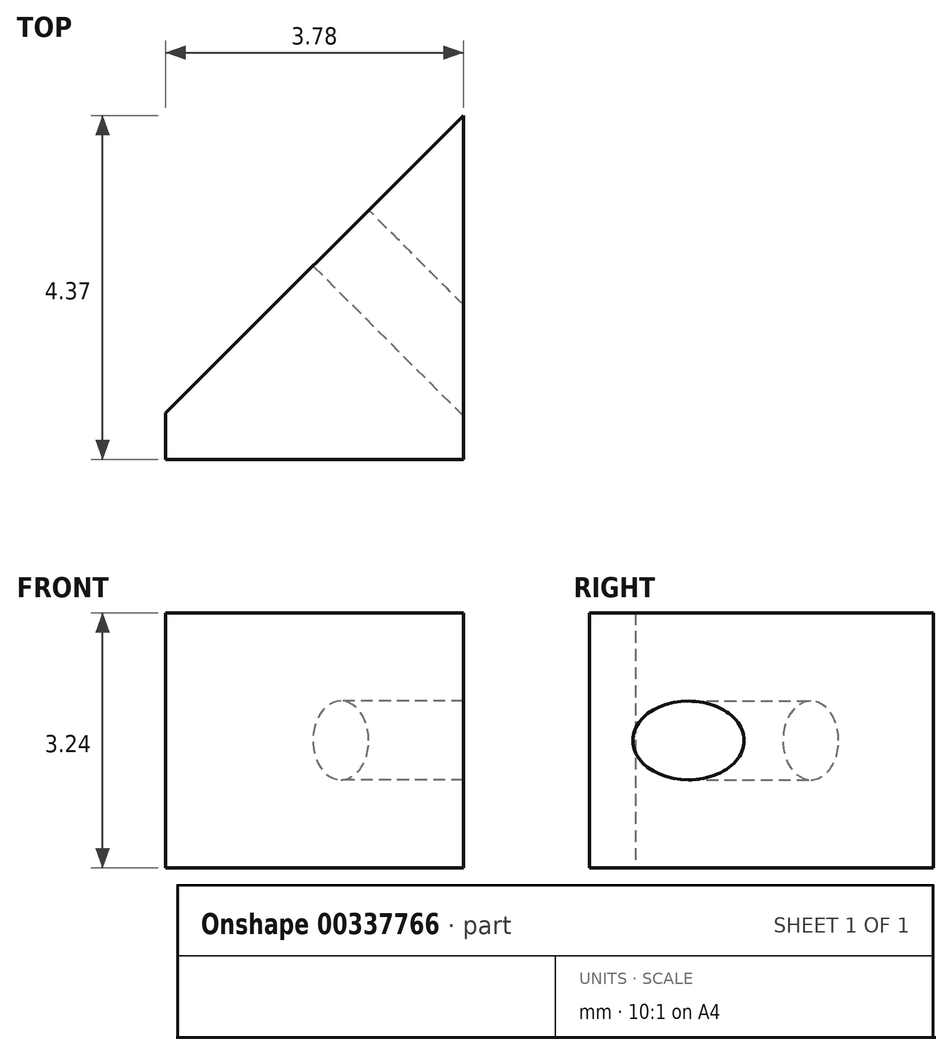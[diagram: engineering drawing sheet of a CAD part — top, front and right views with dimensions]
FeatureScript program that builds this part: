
annotation { "Feature Type Name" : "Feature", "Feature Type Description" : "" }
export const myFeature = defineFeature(function(context is Context, id is Id, definition is map)
    precondition{}
    {
        {
            var Q0;
            Q0=qCreatedBy(makeId("Top.planeOp"),FACE);
            var sketch = newSketch(context, id + "F0", { "sketchPlane" : qUnion([Q0])});
            skLineSegment(sketch, "E0", {"start": v(0, 0) * mm, "end": v(0, 4.37) * mm});
            skLineSegment(sketch, "E1", {"start": v(0, 4.37) * mm, "end": v(-4.37, 0) * mm});
            skLineSegment(sketch, "E2", {"start": v(-4.37, 0) * mm, "end": v(0, 0) * mm});
            skLineSegment(sketch, "E3", {"start": v(-3.78, 0.59) * mm, "end": v(-3.78, 0) * mm});
            skSolve(sketch);
        }
        {
            var Q0;
            {var subQ0=sQuery(id+"F0.wireOp",EDGE,"E0");Q0=makeQuery(id+"F0.imprint","IMPRINT",FACE,{"disambiguationData":[TD([[makeQuery(id+"F0.imprint","IMPRINT",EDGE,{"derivedFrom":subQ0}),1.0]])]});}
            extrude(context, id + "F1", {"entities" : qUnion([Q0]), "depth" : 3.24 * mm});
        }
        {
            var Q0;
            Q0=makeQuery(id+"F1.opExtrude","SWEPT_FACE",FACE,{"disambiguationData":[OSD([sQuery(id+"F0.wireOp",EDGE,"E1")])]});
            var sketch = newSketch(context, id + "F2", { "sketchPlane" : qUnion([Q0])});
            skCircle(sketch, "E4", {"center": v(-0.9, 1.62) * mm, "radius": 0.5 * mm});
            skSolve(sketch);
        }
        {
            var Q0;
            Q0=makeQuery(id+"F2.imprint","IMPRINT",FACE,{"disambiguationData":[TD([[makeQuery(id+"F2.imprint","IMPRINT",EDGE,{"derivedFrom":sQuery(id+"F2.wireOp",EDGE,"E4")}),1.0]])]});
            extrude(context, id + "F3", {"entities" : qUnion([Q0]), "operationType" : NewBodyOperationType.REMOVE, "oppositeDirection" : true, "depth" : 5 * mm, "hasSecondDirection" : true, "secondDirectionOppositeDirection" : false, "secondDirectionDepth" : 25 * mm});
        }
    });
